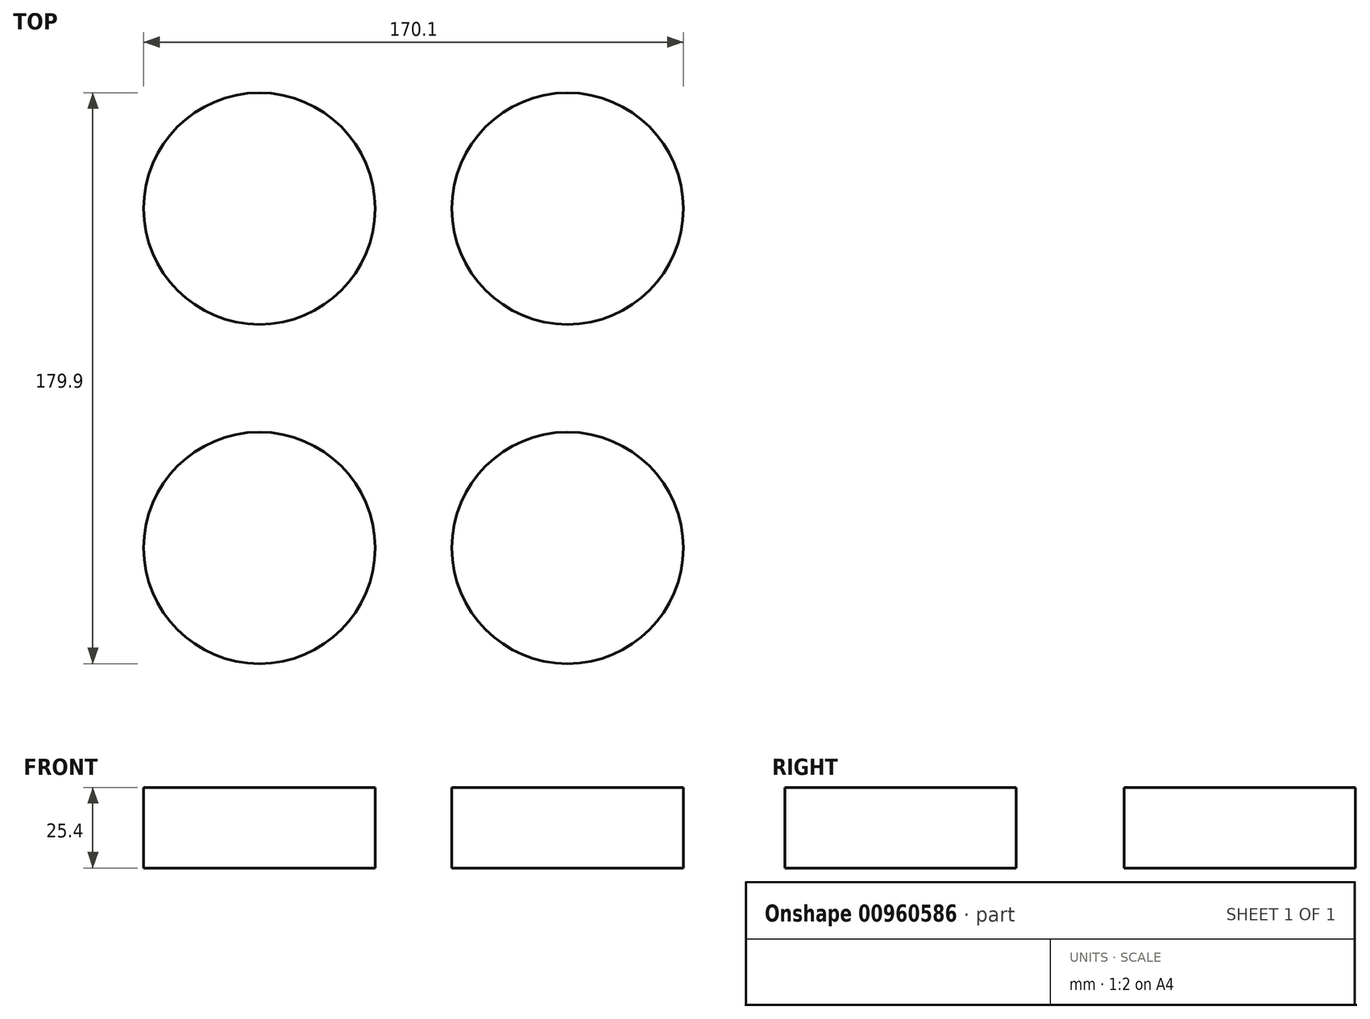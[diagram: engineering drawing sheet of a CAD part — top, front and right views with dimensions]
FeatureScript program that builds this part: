
annotation { "Feature Type Name" : "Feature", "Feature Type Description" : "" }
export const myFeature = defineFeature(function(context is Context, id is Id, definition is map)
    precondition{}
    {
        {
            var Q0;
            Q0=qCreatedBy(makeId("Top.planeOp"),FACE);
            var sketch = newSketch(context, id + "F0", { "sketchPlane" : qUnion([Q0])});
            skCircle(sketch, "E0", {"center": v(48.57, -53.46) * mm, "radius": 36.48 * mm});
            skSolve(sketch);
        }
        {
            var Q0;
            Q0=makeQuery(id+"F0.imprint","IMPRINT",FACE,{"disambiguationData":[TD([[makeQuery(id+"F0.imprint","IMPRINT",EDGE,{"derivedFrom":sQuery(id+"F0.wireOp",EDGE,"E0")}),1.0]])]});
            extrude(context, id + "F1", {"entities" : qUnion([Q0]), "depth" : 25.4 * mm, "offsetDistance" : 25.4 * mm});
        }
        {
            var Q0;
            Q0=makeQuery(id+"F1.opExtrude","SWEPT_BODY",BODY,{"disambiguationData":[OSD([sQuery(id+"F0.wireOp",EDGE,"E0")])]});
            var Q1;
            Q1=qCreatedBy(makeId("Right.planeOp"),FACE);
            mirror(context, id + "F2", {"entities" : qUnion([Q0]), "mirrorPlane" : qUnion([Q1])});
        }
        {
            var Q0;
            Q0=makeQuery(id+"F1.opExtrude","SWEPT_BODY",BODY,{"disambiguationData":[OSD([sQuery(id+"F0.wireOp",EDGE,"E0")])]});
            var Q1;
            Q1=makeQuery(id+"F2.opPattern","COPY",BODY,{"derivedFrom":makeQuery(id+"F1.opExtrude","SWEPT_BODY",BODY,{"disambiguationData":[OSD([sQuery(id+"F0.wireOp",EDGE,"E0")])]}),"instanceName":"1"});
            var Q2;
            Q2=qCreatedBy(makeId("Front.planeOp"),FACE);
            mirror(context, id + "F3", {"entities" : qUnion([Q0, Q1]), "mirrorPlane" : qUnion([Q2])});
        }
    });
